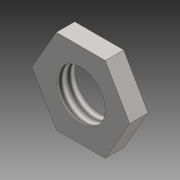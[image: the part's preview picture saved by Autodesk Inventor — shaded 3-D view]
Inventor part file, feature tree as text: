
AUTODESK INVENTOR PART (.ipt)
format: ipt  version: 2016 (Build 200138000, 138)  size: 84,992 bytes
history: native  units: mm
features: extrude x1, thread x1, sketch x1
ambient origin geometry x8: Origin, YZ Plane, XZ Plane, XY Plane, X Axis, Y Axis, Z Axis, Center Point
bodies: Body1 (feature_tree)
feature tree (3):
  extrude  "拉伸2"  Depth=1.5mm TaperAngle=0.0deg
  thread  "螺纹2"  [1 undecoded]
  sketch  "草图1"  dims[d0=4.0mm d7=1.5mm d8=0.0mm d9=10.0mm d10=0.0mm]
note: 1 required parameter value undecoded (feature->parameter linkage not recoverable at this tier; creation-order binding heuristic only, values carry confidence <= 0.55)
